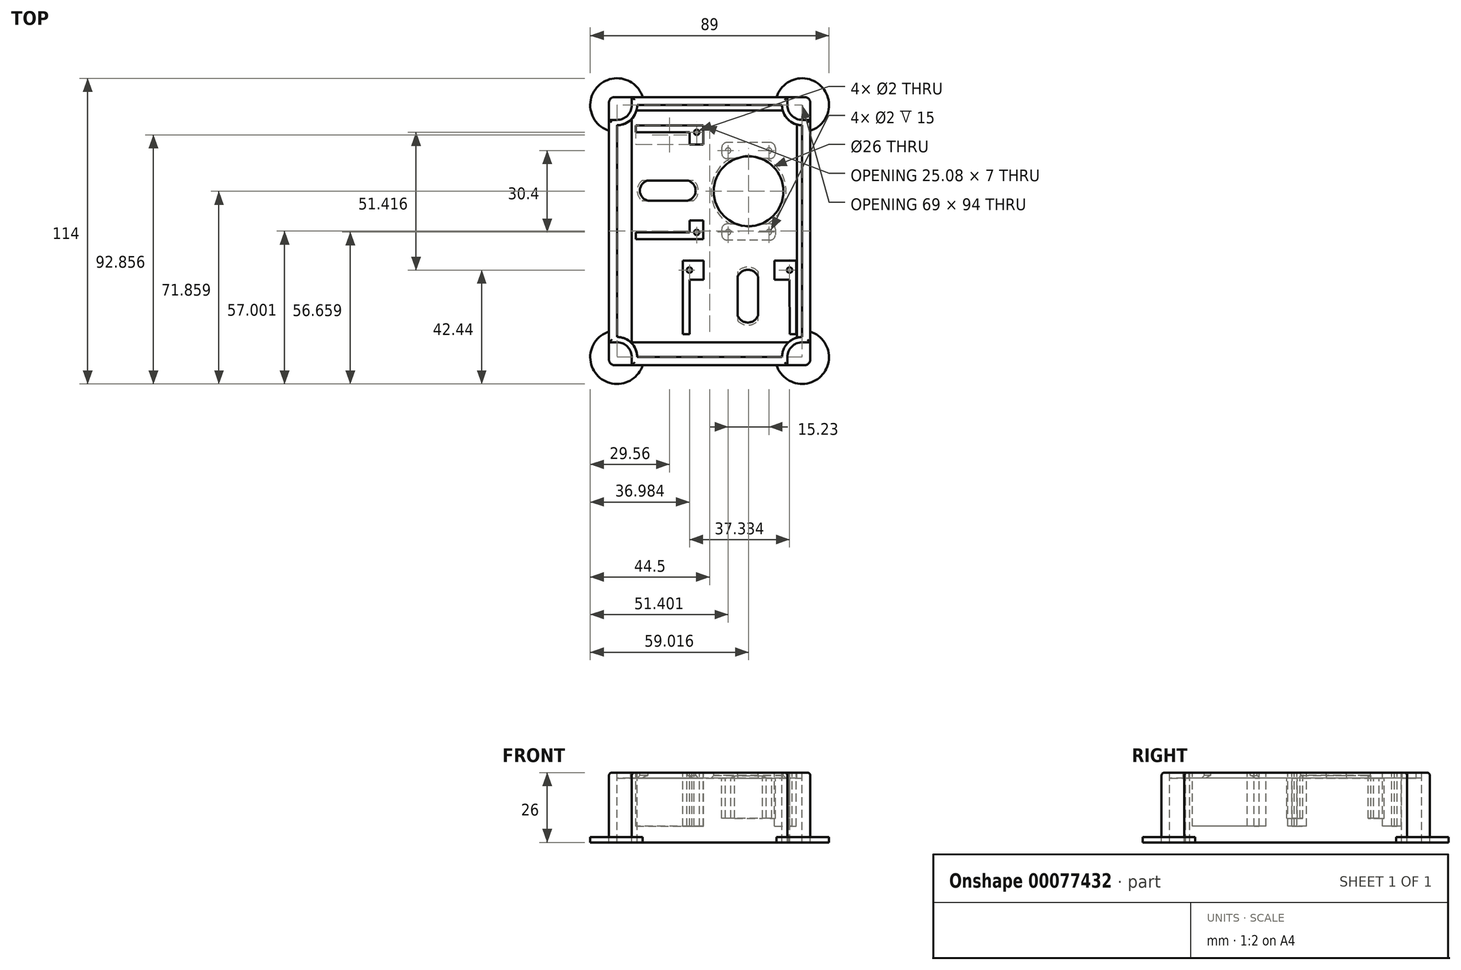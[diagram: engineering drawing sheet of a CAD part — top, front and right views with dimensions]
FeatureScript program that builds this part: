
annotation { "Feature Type Name" : "Feature", "Feature Type Description" : "" }
export const myFeature = defineFeature(function(context is Context, id is Id, definition is map)
    precondition{}
    {
        {
            var Q0;
            Q0=qCreatedBy(makeId("Top.planeOp"),FACE);
            var sketch = newSketch(context, id + "F0", { "sketchPlane" : qUnion([Q0])});
            skLineSegment(sketch, "E0.rect.bottom", {"start": v(-24.52, 14) * mm, "end": v(17.82, 14) * mm});
            skLineSegment(sketch, "E0.rect.top", {"start": v(-24.52, -14) * mm, "end": v(17.82, -14) * mm});
            skLineSegment(sketch, "E0.rect.right", {"start": v(17.82, 14) * mm, "end": v(17.82, -14) * mm});
            skPoint(sketch, "E0.rect.middle", {"position": v(0, 0) * mm});
            skLineSegment(sketch, "E1.rect.bottom", {"start": v(5.3, -4.4) * mm, "end": v(-5.3, -4.4) * mm, "construction": true});
            skLineSegment(sketch, "E1.rect.top", {"start": v(5.3, 6) * mm, "end": v(-5.3, 6) * mm, "construction": true});
            skLineSegment(sketch, "E1.rect.left", {"start": v(5.3, -4.4) * mm, "end": v(5.3, 6) * mm, "construction": true});
            skLineSegment(sketch, "E1.rect.right", {"start": v(-5.3, -4.4) * mm, "end": v(-5.3, 6) * mm, "construction": true});
            skPoint(sketch, "E1.rect.middle", {"position": v(0, 0.8) * mm});
            skLineSegment(sketch, "E2.bottom", {"start": v(-5.3, 6) * mm, "end": v(-3.9, 6) * mm});
            skLineSegment(sketch, "E2.top", {"start": v(-5.3, -4.4) * mm, "end": v(-3.9, -4.4) * mm});
            skLineSegment(sketch, "E2.left", {"start": v(-5.3, 6) * mm, "end": v(-5.3, -4.4) * mm});
            skLineSegment(sketch, "E2.right", {"start": v(-3.9, 6) * mm, "end": v(-3.9, -4.4) * mm});
            skLineSegment(sketch, "E3.1.MirrorCS", {"start": v(3.9, 6) * mm, "end": v(3.9, -4.4) * mm});
            skLineSegment(sketch, "E3.2.MirrorCS", {"start": v(5.3, -4.4) * mm, "end": v(3.9, -4.4) * mm});
            skLineSegment(sketch, "E3.3.MirrorCS", {"start": v(5.3, 6) * mm, "end": v(5.3, -4.4) * mm});
            skLineSegment(sketch, "E3.4.MirrorCS", {"start": v(5.3, 6) * mm, "end": v(3.9, 6) * mm});
            skLineSegment(sketch, "E4", {"start": v(11.9, -2.52) * mm, "end": v(11.9, -9.66) * mm, "construction": true});
            skLineSegment(sketch, "E5", {"start": v(0.13, -12.4) * mm, "end": v(12.65, -12.4) * mm, "construction": true});
            skLineSegment(sketch, "E6", {"start": v(5.3, 0.8) * mm, "end": v(11.55, 0.8) * mm, "construction": true});
            skCircle(sketch, "E7", {"center": v(11.9, -12.4) * mm, "radius": 1.6 * mm});
            skCircle(sketch, "E8", {"center": v(11.9, -12.4) * mm, "radius": 0.75 * mm});
            skLineSegment(sketch, "E9", {"start": v(-16.6, 11.88) * mm, "end": v(-16.6, 4.47) * mm, "construction": true});
            skLineSegment(sketch, "E10", {"start": v(-16.6, 4.47) * mm, "end": v(-16.6, 0.29) * mm, "construction": true});
            skLineSegment(sketch, "E11", {"start": v(-21.75, -2.4) * mm, "end": v(-11.5, -2.4) * mm, "construction": true});
            skCircle(sketch, "E12", {"center": v(-16.6, -2.4) * mm, "radius": 1.6 * mm});
            skCircle(sketch, "E13", {"center": v(-16.6, -2.4) * mm, "radius": 0.45 * mm});
            skLineSegment(sketch, "E14", {"start": v(-24.52, 14) * mm, "end": v(-24.52, -14) * mm});
            skPoint(sketch, "E15.orphan", {"position": v(-17.82, -14) * mm});
            skPoint(sketch, "E0.rect.left.start.orphan", {"position": v(-17.82, 14) * mm});
            skSolve(sketch);
        }
        {
            var Q0;
            Q0=makeQuery(id+"F0.imprint","IMPRINT",FACE,{"disambiguationData":[TD([[makeQuery(id+"F0.imprint","IMPRINT",EDGE,{"derivedFrom":sQuery(id+"F0.wireOp",EDGE,"E0.rect.bottom")}),-1.0]])]});
            var sketch = newSketch(context, id + "F1", { "sketchPlane" : qUnion([Q0])});
            skLineSegment(sketch, "E16.bottom", {"start": v(34.7, 72.06) * mm, "end": v(-30.3, 72.06) * mm});
            skLineSegment(sketch, "E16.top", {"start": v(34.7, -17.94) * mm, "end": v(-30.3, -17.94) * mm});
            skLineSegment(sketch, "E16.left", {"start": v(34.7, 72.06) * mm, "end": v(34.7, -17.94) * mm});
            skLineSegment(sketch, "E16.right", {"start": v(-30.3, 72.06) * mm, "end": v(-30.3, -17.94) * mm});
            skLineSegment(sketch, "E17.bottom", {"start": v(24.22, 56.92) * mm, "end": v(9.22, 56.92) * mm, "construction": true});
            skLineSegment(sketch, "E17.top", {"start": v(24.22, 26.92) * mm, "end": v(9.22, 26.92) * mm, "construction": true});
            skLineSegment(sketch, "E17.left", {"start": v(24.22, 56.92) * mm, "end": v(24.22, 26.92) * mm, "construction": true});
            skLineSegment(sketch, "E17.right", {"start": v(9.22, 56.92) * mm, "end": v(9.22, 26.92) * mm, "construction": true});
            skCircle(sketch, "E18", {"center": v(24.22, 56.92) * mm, "radius": 1 * mm});
            skArc(sketch, "E19", {"start": v(24.22, 54.67) * mm, "mid": v(26.47, 56.92) * mm, "end": v(24.22, 59.17) * mm});
            skCircle(sketch, "E20", {"center": v(9.22, 56.92) * mm, "radius": 1 * mm});
            skArc(sketch, "E21", {"start": v(9.22, 59.17) * mm, "mid": v(6.97, 56.92) * mm, "end": v(9.22, 54.67) * mm});
            skCircle(sketch, "E22", {"center": v(24.22, 26.92) * mm, "radius": 1 * mm});
            skArc(sketch, "E23", {"start": v(24.22, 24.67) * mm, "mid": v(26.47, 26.92) * mm, "end": v(24.22, 29.17) * mm});
            skCircle(sketch, "E24", {"center": v(9.22, 26.92) * mm, "radius": 1 * mm});
            skArc(sketch, "E25", {"start": v(9.22, 29.17) * mm, "mid": v(6.97, 26.92) * mm, "end": v(9.22, 24.67) * mm});
            skLineSegment(sketch, "E26", {"start": v(24.22, 54.67) * mm, "end": v(9.22, 54.67) * mm});
            skLineSegment(sketch, "E27", {"start": v(24.22, 29.17) * mm, "end": v(9.22, 29.17) * mm});
            skLineSegment(sketch, "E28.0.MirrorCS", {"start": v(24.22, 59.17) * mm, "end": v(9.22, 59.17) * mm});
            skLineSegment(sketch, "E29.0.MirrorCS", {"start": v(24.22, 24.67) * mm, "end": v(9.22, 24.67) * mm});
            skLineSegment(sketch, "E30", {"start": v(24.22, 56.92) * mm, "end": v(9.22, 26.92) * mm, "construction": true});
            skLineSegment(sketch, "E31", {"start": v(9.22, 56.92) * mm, "end": v(24.22, 26.92) * mm, "construction": true});
            skCircle(sketch, "E32", {"center": v(16.72, 41.92) * mm, "radius": 10 * mm});
            skLineSegment(sketch, "E33", {"start": v(16.72, 41.92) * mm, "end": v(-32.46, 41.92) * mm, "construction": true});
            skLineSegment(sketch, "E34", {"start": v(16.72, 41.92) * mm, "end": v(16.72, -38.62) * mm, "construction": true});
            skSolve(sketch);
        }
        {
            var Q0;
            Q0=qCreatedBy(makeId("Top.planeOp"),FACE);
            cPlane(context, id + "F2", {"entities" : qUnion([Q0]), "cplaneType" : CPlaneType.OFFSET, "offset" : 22.03 * mm, "width" : 150 * mm, "height" : 150 * mm});
        }
        {
            var Q0;
            Q0=qCreatedBy(makeId("Top.planeOp"),FACE);
            cPlane(context, id + "F3", {"entities" : qUnion([Q0]), "cplaneType" : CPlaneType.OFFSET, "offset" : 12.28 * mm, "width" : 150 * mm, "height" : 150 * mm});
        }
        {
            var Q0;
            Q0=qCreatedBy(id+"F3.planeOp",FACE);
            var sketch = newSketch(context, id + "F4", { "sketchPlane" : qUnion([Q0])});
            skLineSegment(sketch, "E35.0.0", {"start": v(34.7, 72.06) * mm, "end": v(34.7, -17.94) * mm});
            skLineSegment(sketch, "E35.0.1", {"start": v(34.7, 72.06) * mm, "end": v(-30.3, 72.06) * mm});
            skLineSegment(sketch, "E35.0.2", {"start": v(-30.3, 72.06) * mm, "end": v(-30.3, -17.94) * mm});
            skLineSegment(sketch, "E35.0.3", {"start": v(34.7, -17.94) * mm, "end": v(-30.3, -17.94) * mm});
            skLineSegment(sketch, "E36.bottom", {"start": v(-30.3, -17.94) * mm, "end": v(34.7, -17.94) * mm});
            skLineSegment(sketch, "E36.top", {"start": v(-30.3, 72.06) * mm, "end": v(34.7, 72.06) * mm});
            skLineSegment(sketch, "E36.left", {"start": v(-30.3, -17.94) * mm, "end": v(-30.3, 72.06) * mm});
            skLineSegment(sketch, "E36.right", {"start": v(34.7, -17.94) * mm, "end": v(34.7, 72.06) * mm});
            skSolve(sketch);
        }
        {
            var Q0;
            Q0=qCreatedBy(id+"F2.planeOp",FACE);
            var sketch = newSketch(context, id + "F5", { "sketchPlane" : qUnion([Q0])});
            skLineSegment(sketch, "E37.bottom", {"start": v(37.7, 77.06) * mm, "end": v(-33.3, 77.06) * mm});
            skLineSegment(sketch, "E37.top", {"start": v(37.7, -22.94) * mm, "end": v(-33.3, -22.94) * mm});
            skLineSegment(sketch, "E37.left", {"start": v(39.7, 75.06) * mm, "end": v(39.7, -20.94) * mm});
            skLineSegment(sketch, "E37.right", {"start": v(-35.3, 75.06) * mm, "end": v(-35.3, -20.94) * mm});
            skLineSegment(sketch, "E38.0", {"start": v(34.7, 72.06) * mm, "end": v(-30.3, 72.06) * mm});
            skLineSegment(sketch, "E38.1", {"start": v(-30.3, 72.06) * mm, "end": v(-30.3, -17.94) * mm});
            skLineSegment(sketch, "E38.2", {"start": v(34.7, -17.94) * mm, "end": v(-30.3, -17.94) * mm});
            skLineSegment(sketch, "E38.3", {"start": v(34.7, 72.06) * mm, "end": v(34.7, -17.94) * mm});
            skCircle(sketch, "E39", {"center": v(-30.3, 72.06) * mm, "radius": 1.25 * mm});
            skCircle(sketch, "E40", {"center": v(34.7, 72.06) * mm, "radius": 1.25 * mm});
            skCircle(sketch, "E41", {"center": v(-30.3, -17.94) * mm, "radius": 1.25 * mm});
            skCircle(sketch, "E42", {"center": v(34.7, -17.94) * mm, "radius": 1.25 * mm});
            skLineSegment(sketch, "E43.0", {"start": v(-32.3, 74.06) * mm, "end": v(-32.3, -19.94) * mm});
            skLineSegment(sketch, "E43.1", {"start": v(36.7, 74.06) * mm, "end": v(-32.3, 74.06) * mm});
            skLineSegment(sketch, "E43.2", {"start": v(36.7, 74.06) * mm, "end": v(36.7, -19.94) * mm});
            skLineSegment(sketch, "E43.3", {"start": v(36.7, -19.94) * mm, "end": v(-32.3, -19.94) * mm});
            skArc(sketch, "E44", {"start": v(-32.3, 68.56) * mm, "mid": v(-28.41, 70.17) * mm, "end": v(-26.8, 74.06) * mm});
            skArc(sketch, "E45", {"start": v(31.2, 74.06) * mm, "mid": v(32.81, 70.17) * mm, "end": v(36.7, 68.56) * mm});
            skArc(sketch, "E46", {"start": v(-26.8, -19.94) * mm, "mid": v(-28.41, -16.05) * mm, "end": v(-32.3, -14.44) * mm});
            skArc(sketch, "E47", {"start": v(36.7, -14.44) * mm, "mid": v(32.81, -16.05) * mm, "end": v(31.2, -19.94) * mm});
            skLineSegment(sketch, "E48", {"start": v(36.7, 68.56) * mm, "end": v(39.7, 68.56) * mm});
            skLineSegment(sketch, "E49", {"start": v(-32.3, 68.56) * mm, "end": v(-35.3, 68.56) * mm});
            skPoint(sketch, "E50.orphan", {"position": v(-35.3, 69.45) * mm});
            skLineSegment(sketch, "E51", {"start": v(-26.8, 74.06) * mm, "end": v(-26.8, -17.94) * mm});
            skLineSegment(sketch, "E52", {"start": v(-30.3, -14.44) * mm, "end": v(39.7, -14.44) * mm});
            skLineSegment(sketch, "E53", {"start": v(31.2, -17.94) * mm, "end": v(31.2, 77.06) * mm});
            skLineSegment(sketch, "E54", {"start": v(31.2, -19.94) * mm, "end": v(31.2, -22.94) * mm});
            skLineSegment(sketch, "E55", {"start": v(-32.3, -14.44) * mm, "end": v(-35.3, -14.44) * mm});
            skLineSegment(sketch, "E56.trimOffspring", {"start": v(-26.8, -19.94) * mm, "end": v(-26.8, -22.94) * mm});
            skLineSegment(sketch, "E57", {"start": v(-26.8, 74.06) * mm, "end": v(-26.8, 77.06) * mm});
            skPoint(sketch, "E58.visualSharp", {"position": v(-35.3, 77.06) * mm});
            skArc(sketch, "E58.filletArc", {"start": v(-33.3, 77.06) * mm, "mid": v(-34.71, 76.48) * mm, "end": v(-35.3, 75.06) * mm});
            skPoint(sketch, "E59.visualSharp", {"position": v(39.7, 77.06) * mm});
            skArc(sketch, "E59.filletArc", {"start": v(39.7, 75.06) * mm, "mid": v(39.11, 76.48) * mm, "end": v(37.7, 77.06) * mm});
            skPoint(sketch, "E60.visualSharp", {"position": v(-35.3, -22.94) * mm});
            skArc(sketch, "E60.filletArc", {"start": v(-35.3, -20.94) * mm, "mid": v(-34.71, -22.35) * mm, "end": v(-33.3, -22.94) * mm});
            skPoint(sketch, "E61.visualSharp", {"position": v(39.7, -22.94) * mm});
            skArc(sketch, "E61.filletArc", {"start": v(37.7, -22.94) * mm, "mid": v(39.11, -22.35) * mm, "end": v(39.7, -20.94) * mm});
            skArc(sketch, "E62", {"start": v(-22.76, 77.06) * mm, "mid": v(-39.37, 81.13) * mm, "end": v(-35.3, 64.52) * mm});
            skArc(sketch, "E63", {"start": v(39.7, 64.52) * mm, "mid": v(43.77, 81.13) * mm, "end": v(27.16, 77.06) * mm});
            skArc(sketch, "E64", {"start": v(27.16, -22.94) * mm, "mid": v(43.77, -27) * mm, "end": v(39.7, -10.4) * mm});
            skArc(sketch, "E65", {"start": v(-35.3, -10.4) * mm, "mid": v(-39.37, -27) * mm, "end": v(-22.76, -22.94) * mm});
            skSolve(sketch);
        }
        {
            var Q0;
            Q0=qCreatedBy(id+"F2.planeOp",FACE);
            var sketch = newSketch(context, id + "F6", { "sketchPlane" : qUnion([Q0])});
            skLineSegment(sketch, "E66.0", {"start": v(37.7, 77.06) * mm, "end": v(-33.3, 77.06) * mm});
            skLineSegment(sketch, "E66.1", {"start": v(37.7, -22.94) * mm, "end": v(-33.3, -22.94) * mm});
            skLineSegment(sketch, "E66.2", {"start": v(39.7, 75.06) * mm, "end": v(39.7, -20.94) * mm});
            skLineSegment(sketch, "E66.3", {"start": v(-35.3, 75.06) * mm, "end": v(-35.3, -20.94) * mm});
            skLineSegment(sketch, "E66.4", {"start": v(34.7, 72.06) * mm, "end": v(-30.3, 72.06) * mm});
            skLineSegment(sketch, "E66.5", {"start": v(-30.3, 72.06) * mm, "end": v(-30.3, -17.94) * mm});
            skLineSegment(sketch, "E66.6", {"start": v(34.7, -17.94) * mm, "end": v(-30.3, -17.94) * mm});
            skLineSegment(sketch, "E66.7", {"start": v(34.7, 72.06) * mm, "end": v(34.7, -17.94) * mm});
            skCircle(sketch, "E66.8", {"center": v(-30.3, 72.06) * mm, "radius": 1.25 * mm});
            skCircle(sketch, "E66.9", {"center": v(34.7, 72.06) * mm, "radius": 1.25 * mm});
            skCircle(sketch, "E66.10", {"center": v(-30.3, -17.94) * mm, "radius": 1.25 * mm});
            skCircle(sketch, "E66.11", {"center": v(34.7, -17.94) * mm, "radius": 1.25 * mm});
            skLineSegment(sketch, "E66.12", {"start": v(-32.3, 74.06) * mm, "end": v(-32.3, -19.94) * mm});
            skLineSegment(sketch, "E66.13", {"start": v(36.7, 74.06) * mm, "end": v(-32.3, 74.06) * mm});
            skLineSegment(sketch, "E66.14", {"start": v(36.7, 74.06) * mm, "end": v(36.7, -19.94) * mm});
            skLineSegment(sketch, "E66.15", {"start": v(36.7, -19.94) * mm, "end": v(-32.3, -19.94) * mm});
            skArc(sketch, "E66.16", {"start": v(-32.3, 68.56) * mm, "mid": v(-28.41, 70.17) * mm, "end": v(-26.8, 74.06) * mm});
            skArc(sketch, "E66.17", {"start": v(31.2, 74.06) * mm, "mid": v(32.81, 70.17) * mm, "end": v(36.7, 68.56) * mm});
            skArc(sketch, "E66.18", {"start": v(-26.8, -19.94) * mm, "mid": v(-28.41, -16.05) * mm, "end": v(-32.3, -14.44) * mm});
            skArc(sketch, "E66.19", {"start": v(36.7, -14.44) * mm, "mid": v(32.81, -16.05) * mm, "end": v(31.2, -19.94) * mm});
            skLineSegment(sketch, "E66.20", {"start": v(36.7, 68.56) * mm, "end": v(39.7, 68.56) * mm});
            skLineSegment(sketch, "E66.21", {"start": v(-32.3, 68.56) * mm, "end": v(-35.3, 68.56) * mm});
            skPoint(sketch, "E66.22", {"position": v(-35.3, 69.45) * mm});
            skLineSegment(sketch, "E66.23", {"start": v(-26.8, 72.06) * mm, "end": v(-26.8, -17.94) * mm});
            skLineSegment(sketch, "E66.24", {"start": v(-30.3, -14.44) * mm, "end": v(39.7, -14.44) * mm});
            skLineSegment(sketch, "E66.26", {"start": v(31.2, -19.94) * mm, "end": v(31.2, -22.94) * mm});
            skLineSegment(sketch, "E66.27", {"start": v(-32.3, -14.44) * mm, "end": v(-35.3, -14.44) * mm});
            skLineSegment(sketch, "E66.28", {"start": v(-26.8, -19.94) * mm, "end": v(-26.8, -22.94) * mm});
            skLineSegment(sketch, "E66.29", {"start": v(-26.8, 74.06) * mm, "end": v(-26.8, 77.06) * mm});
            skPoint(sketch, "E66.30", {"position": v(-35.3, 77.06) * mm});
            skArc(sketch, "E66.31", {"start": v(-33.3, 77.06) * mm, "mid": v(-34.71, 76.48) * mm, "end": v(-35.3, 75.06) * mm});
            skPoint(sketch, "E66.32", {"position": v(39.7, 77.06) * mm});
            skArc(sketch, "E66.33", {"start": v(39.7, 75.06) * mm, "mid": v(39.11, 76.48) * mm, "end": v(37.7, 77.06) * mm});
            skPoint(sketch, "E66.34", {"position": v(-35.3, -22.94) * mm});
            skArc(sketch, "E66.35", {"start": v(-35.3, -20.94) * mm, "mid": v(-34.71, -22.35) * mm, "end": v(-33.3, -22.94) * mm});
            skPoint(sketch, "E66.36", {"position": v(39.7, -22.94) * mm});
            skArc(sketch, "E66.37", {"start": v(37.7, -22.94) * mm, "mid": v(39.11, -22.35) * mm, "end": v(39.7, -20.94) * mm});
            skPoint(sketch, "E67.orphan", {"position": v(-26.8, 74.06) * mm});
            skLineSegment(sketch, "E68.trimOffspring", {"start": v(31.2, 74.06) * mm, "end": v(31.2, 77.06) * mm});
            skArc(sketch, "E69.0", {"start": v(-32.3, 66.56) * mm, "mid": v(-27, 68.76) * mm, "end": v(-24.8, 74.06) * mm});
            skArc(sketch, "E70.0", {"start": v(29.2, 74.06) * mm, "mid": v(31.4, 68.76) * mm, "end": v(36.7, 66.56) * mm});
            skArc(sketch, "E71.0", {"start": v(-24.8, -19.94) * mm, "mid": v(-27, -14.64) * mm, "end": v(-32.3, -12.44) * mm});
            skArc(sketch, "E72.0", {"start": v(36.7, -12.44) * mm, "mid": v(34.28, -12.84) * mm, "end": v(32.12, -14) * mm});
            skLineSegment(sketch, "E73.bottom", {"start": v(-5.32, 9) * mm, "end": v(0, 9) * mm});
            skLineSegment(sketch, "E73.left", {"start": v(-5.32, 9) * mm, "end": v(-5.32, -14) * mm});
            skLineSegment(sketch, "E73.right", {"start": v(32.02, 9) * mm, "end": v(32.02, -11.4) * mm});
            skLineSegment(sketch, "E74.left", {"start": v(-7.82, 14) * mm, "end": v(-7.82, 12.5) * mm});
            skLineSegment(sketch, "E75", {"start": v(-5.32, 9) * mm, "end": v(-5.32, 11.73) * mm, "construction": true});
            skLineSegment(sketch, "E76", {"start": v(32.02, 9) * mm, "end": v(32.02, 11.5) * mm, "construction": true});
            skLineSegment(sketch, "E77.bottom", {"start": v(-5.2, 63.92) * mm, "end": v(-25.28, 63.92) * mm});
            skLineSegment(sketch, "E77.top", {"start": v(-5.2, 26.58) * mm, "end": v(-25.28, 26.58) * mm});
            skLineSegment(sketch, "E77.left", {"start": v(-5.2, 63.92) * mm, "end": v(-5.2, 59.42) * mm});
            skLineSegment(sketch, "E78", {"start": v(-5.2, 45.99) * mm, "end": v(0, 45.99) * mm, "construction": true});
            skLineSegment(sketch, "E79", {"start": v(-2.6, 45.99) * mm, "end": v(-2.6, 24.96) * mm, "construction": true});
            skLineSegment(sketch, "E80", {"start": v(-2.6, 24.96) * mm, "end": v(-2.6, 64.48) * mm, "construction": true});
            skLineSegment(sketch, "E81", {"start": v(-5.2, 63.92) * mm, "end": v(-2.6, 63.92) * mm, "construction": true});
            skLineSegment(sketch, "E82", {"start": v(-5.2, 26.58) * mm, "end": v(-1.42, 26.58) * mm, "construction": true});
            skCircle(sketch, "E83", {"center": v(-2.6, 63.92) * mm, "radius": 1 * mm});
            skLineSegment(sketch, "E84", {"start": v(-25.28, 66.42) * mm, "end": v(-25.28, 63.92) * mm});
            skLineSegment(sketch, "E85.trimOffspring", {"start": v(-25.28, 26.58) * mm, "end": v(-25.28, 24.08) * mm});
            skLineSegment(sketch, "E86", {"start": v(-7.82, -11.39) * mm, "end": v(34.52, -11.39) * mm});
            skLineSegment(sketch, "E87.left", {"start": v(-7.82, 14) * mm, "end": v(-7.82, 16) * mm});
            skLineSegment(sketch, "E87.right", {"start": v(34.52, 14) * mm, "end": v(34.52, 16) * mm});
            skLineSegment(sketch, "E88", {"start": v(12.87, 12.5) * mm, "end": v(12.87, 16) * mm, "construction": true});
            skLineSegment(sketch, "E89", {"start": v(12.87, 12.5) * mm, "end": v(32.96, 12.5) * mm, "construction": true});
            skLineSegment(sketch, "E90", {"start": v(32.96, 12.5) * mm, "end": v(-7.82, 12.5) * mm, "construction": true});
            skCircle(sketch, "E91", {"center": v(-5.32, 12.5) * mm, "radius": 1 * mm});
            skCircle(sketch, "E92", {"center": v(32.02, 12.5) * mm, "radius": 1 * mm});
            skLineSegment(sketch, "E93.left", {"start": v(0, 16) * mm, "end": v(0, 9) * mm});
            skLineSegment(sketch, "E93.right", {"start": v(26.43, 16) * mm, "end": v(26.43, 9) * mm});
            skLineSegment(sketch, "E94.trimOffspring", {"start": v(-0.2, 31.08) * mm, "end": v(-0.2, 24.08) * mm});
            skLineSegment(sketch, "E95.trimOffspring", {"start": v(26.43, 9) * mm, "end": v(32.02, 9) * mm});
            skPoint(sketch, "E96.orphan", {"position": v(12.87, 9) * mm});
            skLineSegment(sketch, "E97", {"start": v(32.02, 9) * mm, "end": v(32.1, -11.4) * mm});
            skLineSegment(sketch, "E98", {"start": v(34.52, 14) * mm, "end": v(34.52, -11.39) * mm});
            skLineSegment(sketch, "E99", {"start": v(34.52, -11.39) * mm, "end": v(32.02, -11.4) * mm});
            skLineSegment(sketch, "E100", {"start": v(26.43, 14) * mm, "end": v(26.43, 16) * mm});
            skLineSegment(sketch, "E101", {"start": v(-25.28, 26.58) * mm, "end": v(-5.2, 26.58) * mm});
            skLineSegment(sketch, "E102", {"start": v(-5.2, 26.58) * mm, "end": v(-5.2, 31.08) * mm});
            skLineSegment(sketch, "E103", {"start": v(-25.28, 66.42) * mm, "end": v(-0.2, 66.42) * mm});
            skLineSegment(sketch, "E104", {"start": v(-0.2, 66.42) * mm, "end": v(-0.2, 59.42) * mm});
            skLineSegment(sketch, "E105", {"start": v(-25.28, 24.08) * mm, "end": v(-0.2, 24.08) * mm});
            skLineSegment(sketch, "E106", {"start": v(-25.28, 24.08) * mm, "end": v(-28.2, 24.08) * mm, "construction": true});
            skPoint(sketch, "E107.orphan", {"position": v(-7.82, -14) * mm});
            skLineSegment(sketch, "E108", {"start": v(-7.82, -11.39) * mm, "end": v(-7.82, -14) * mm});
            skLineSegment(sketch, "E109", {"start": v(-7.82, -14) * mm, "end": v(-5.32, -14) * mm});
            skLineSegment(sketch, "E110", {"start": v(-7.82, -14) * mm, "end": v(-7.82, -11.39) * mm});
            skLineSegment(sketch, "E111", {"start": v(-7.82, -11.39) * mm, "end": v(-7.82, 12.5) * mm});
            skLineSegment(sketch, "E112", {"start": v(-7.82, 12.5) * mm, "end": v(-7.82, -14) * mm});
            skLineSegment(sketch, "E113", {"start": v(-5.32, -14) * mm, "end": v(-5.32, 9) * mm});
            skLineSegment(sketch, "E114", {"start": v(0, 9) * mm, "end": v(0, 14) * mm});
            skLineSegment(sketch, "E115", {"start": v(0, 9) * mm, "end": v(0, 16) * mm});
            skLineSegment(sketch, "E116", {"start": v(0, 16) * mm, "end": v(-7.82, 16) * mm});
            skArc(sketch, "E117.trimOffspring", {"start": v(31.6, -14.44) * mm, "mid": v(29.83, -16.94) * mm, "end": v(29.2, -19.94) * mm});
            skPoint(sketch, "E118.0.end.orphan", {"position": v(34.52, -12.76) * mm});
            skLineSegment(sketch, "E119", {"start": v(31.6, -14.44) * mm, "end": v(32.12, -14) * mm});
            skLineSegment(sketch, "E120", {"start": v(-25.28, 66.42) * mm, "end": v(-28.2, 66.42) * mm, "construction": true});
            skLineSegment(sketch, "E121.trimOffspring", {"start": v(26.43, 16) * mm, "end": v(34.52, 16) * mm});
            skLineSegment(sketch, "E122", {"start": v(26.43, 9) * mm, "end": v(26.43, 16) * mm});
            skLineSegment(sketch, "E123", {"start": v(-5.2, 31.08) * mm, "end": v(0, 31.08) * mm});
            skLineSegment(sketch, "E124.trimOffspring", {"start": v(-5.2, 31.08) * mm, "end": v(-5.2, 26.58) * mm});
            skLineSegment(sketch, "E125", {"start": v(-0.2, 59.42) * mm, "end": v(-5.2, 59.42) * mm});
            skCircle(sketch, "E126", {"center": v(-2.6, 26.58) * mm, "radius": 1 * mm});
            skSolve(sketch);
        }
        {
            var Q0;
            {var subQ1=sQuery(id+"F6.wireOp",EDGE,"E66.23");var subQ3=sQuery(id+"F6.wireOp",EDGE,"E66.6");var subQ5=makeQuery(id+"F6.imprint","INTERSECT",VERTEX,{"derivedFrom":[subQ3,subQ1]});Q0=makeQuery(id+"F6.imprint","IMPRINT",FACE,{"disambiguationData":[TD([[makeQuery(id+"F6.imprint","IMPRINT",EDGE,{"disambiguationData":[TD([[subQ5,1.0]])],"derivedFrom":subQ3}),-1.0]])]});}
            var Q1;
            {var subQ1=sQuery(id+"F6.wireOp",EDGE,"E66.23");var subQ3=sQuery(id+"F6.wireOp",EDGE,"E66.6");var subQ5=makeQuery(id+"F6.imprint","INTERSECT",VERTEX,{"derivedFrom":[subQ3,subQ1]});Q1=makeQuery(id+"F6.imprint","IMPRINT",FACE,{"disambiguationData":[TD([[makeQuery(id+"F6.imprint","IMPRINT",EDGE,{"disambiguationData":[TD([[subQ5,1.0]])],"derivedFrom":subQ3}),-1.0]])]});}
            var Q2;
            {var subQ3=sQuery(id+"F6.wireOp",EDGE,"E66.29");Q2=makeQuery(id+"F6.imprint","IMPRINT",FACE,{"disambiguationData":[TD([[makeQuery(id+"F6.imprint","IMPRINT",EDGE,{"derivedFrom":subQ3}),-1.0]])]});}
            var Q3;
            {var subQ1=sQuery(id+"F6.wireOp",EDGE,"E66.26");Q3=makeQuery(id+"F6.imprint","IMPRINT",FACE,{"disambiguationData":[TD([[makeQuery(id+"F6.imprint","IMPRINT",EDGE,{"derivedFrom":subQ1}),-1.0]])]});}
            var Q4;
            {var subQ5=sQuery(id+"F6.wireOp",EDGE,"E66.20");Q4=makeQuery(id+"F6.imprint","IMPRINT",FACE,{"disambiguationData":[TD([[makeQuery(id+"F6.imprint","IMPRINT",EDGE,{"derivedFrom":subQ5}),-1.0]])]});}
            var Q5;
            {var subQ1=sQuery(id+"F6.wireOp",EDGE,"E66.21");Q5=makeQuery(id+"F6.imprint","IMPRINT",FACE,{"disambiguationData":[TD([[makeQuery(id+"F6.imprint","IMPRINT",EDGE,{"derivedFrom":subQ1}),1.0]])]});}
            var Q6;
            {var subQ1=sQuery(id+"F6.wireOp",EDGE,"E66.5");var subQ5=sQuery(id+"F6.wireOp",EDGE,"E66.16");var subQ6=makeQuery(id+"F6.imprint","INTERSECT",VERTEX,{"derivedFrom":[subQ1,subQ5]});Q6=makeQuery(id+"F6.imprint","IMPRINT",FACE,{"disambiguationData":[TD([[makeQuery(id+"F6.imprint","IMPRINT",EDGE,{"disambiguationData":[TD([[subQ6,-1.0]])],"derivedFrom":subQ1}),-1.0]])]});}
            var Q7;
            {var subQ1=sQuery(id+"F6.wireOp",EDGE,"E66.23");var subQ5=sQuery(id+"F6.wireOp",EDGE,"E66.4");var subQ6=makeQuery(id+"F6.imprint","INTERSECT",VERTEX,{"derivedFrom":[subQ5,subQ1]});Q7=makeQuery(id+"F6.imprint","IMPRINT",FACE,{"disambiguationData":[TD([[makeQuery(id+"F6.imprint","IMPRINT",EDGE,{"disambiguationData":[TD([[subQ6,-1.0]])],"derivedFrom":subQ5}),1.0]])]});}
            var Q8;
            {var subQ1=sQuery(id+"F6.wireOp",EDGE,"E66.23");var subQ3=sQuery(id+"F6.wireOp",EDGE,"E66.4");var subQ5=makeQuery(id+"F6.imprint","INTERSECT",VERTEX,{"derivedFrom":[subQ3,subQ1]});Q8=makeQuery(id+"F6.imprint","IMPRINT",FACE,{"disambiguationData":[TD([[makeQuery(id+"F6.imprint","IMPRINT",EDGE,{"disambiguationData":[TD([[subQ5,1.0]])],"derivedFrom":subQ3}),1.0]])]});}
            var Q9;
            {var subQ1=sQuery(id+"F6.wireOp",EDGE,"E66.4");var subQ7=makeQuery(id+"F6.imprint","INTERSECT",VERTEX,{"derivedFrom":[subQ1,sQuery(id+"F6.wireOp",EDGE,"E66.23")]});Q9=makeQuery(id+"F6.imprint","IMPRINT",FACE,{"disambiguationData":[TD([[makeQuery(id+"F6.imprint","IMPRINT",EDGE,{"disambiguationData":[TD([[subQ7,1.0]])],"derivedFrom":subQ1}),-1.0]])]});}
            var Q10;
            {var subQ1=sQuery(id+"F6.wireOp",EDGE,"E66.4");var subQ7=makeQuery(id+"F6.imprint","INTERSECT",VERTEX,{"derivedFrom":[subQ1,sQuery(id+"F6.wireOp",EDGE,"E66.23")]});Q10=makeQuery(id+"F6.imprint","IMPRINT",FACE,{"disambiguationData":[TD([[makeQuery(id+"F6.imprint","IMPRINT",EDGE,{"disambiguationData":[TD([[subQ7,1.0]])],"derivedFrom":subQ1}),-1.0]])]});}
            var Q11;
            {var subQ1=sQuery(id+"F6.wireOp",EDGE,"E66.23");var subQ3=sQuery(id+"F6.wireOp",EDGE,"E66.4");var subQ5=makeQuery(id+"F6.imprint","INTERSECT",VERTEX,{"derivedFrom":[subQ3,subQ1]});Q11=makeQuery(id+"F6.imprint","IMPRINT",FACE,{"disambiguationData":[TD([[makeQuery(id+"F6.imprint","IMPRINT",EDGE,{"disambiguationData":[TD([[subQ5,1.0]])],"derivedFrom":subQ3}),1.0]])]});}
            var Q12;
            {var subQ1=sQuery(id+"F6.wireOp",EDGE,"E66.23");var subQ3=sQuery(id+"F6.wireOp",EDGE,"E66.4");var subQ5=makeQuery(id+"F6.imprint","INTERSECT",VERTEX,{"derivedFrom":[subQ3,subQ1]});Q12=makeQuery(id+"F6.imprint","IMPRINT",FACE,{"disambiguationData":[TD([[makeQuery(id+"F6.imprint","IMPRINT",EDGE,{"disambiguationData":[TD([[subQ5,1.0]])],"derivedFrom":subQ3}),1.0]])]});}
            var Q13;
            {var subQ1=sQuery(id+"F6.wireOp",EDGE,"E66.7");var subQ5=sQuery(id+"F6.wireOp",EDGE,"E66.17");var subQ6=makeQuery(id+"F6.imprint","INTERSECT",VERTEX,{"derivedFrom":[subQ1,subQ5]});Q13=makeQuery(id+"F6.imprint","IMPRINT",FACE,{"disambiguationData":[TD([[makeQuery(id+"F6.imprint","IMPRINT",EDGE,{"disambiguationData":[TD([[subQ6,-1.0]])],"derivedFrom":subQ1}),1.0]])]});}
            var Q14;
            {var subQ0=sQuery(id+"F6.wireOp",EDGE,"E72.0");var subQ1=sQuery(id+"F6.wireOp",EDGE,"E66.7");var subQ2=makeQuery(id+"F6.imprint","INTERSECT",VERTEX,{"derivedFrom":[subQ1,subQ0]});Q14=makeQuery(id+"F6.imprint","IMPRINT",FACE,{"disambiguationData":[TD([[makeQuery(id+"F6.imprint","IMPRINT",EDGE,{"disambiguationData":[TD([[subQ2,-1.0]])],"derivedFrom":subQ1}),1.0]])]});}
            var Q15;
            {var subQ0=sQuery(id+"F6.wireOp",EDGE,"E119");Q15=makeQuery(id+"F6.imprint","IMPRINT",FACE,{"disambiguationData":[TD([[makeQuery(id+"F6.imprint","IMPRINT",EDGE,{"derivedFrom":subQ0}),-1.0]])]});}
            var Q16;
            {var subQ1=sQuery(id+"F6.wireOp",EDGE,"E66.23");var subQ3=sQuery(id+"F6.wireOp",EDGE,"E66.6");var subQ5=makeQuery(id+"F6.imprint","INTERSECT",VERTEX,{"derivedFrom":[subQ3,subQ1]});Q16=makeQuery(id+"F6.imprint","IMPRINT",FACE,{"disambiguationData":[TD([[makeQuery(id+"F6.imprint","IMPRINT",EDGE,{"disambiguationData":[TD([[subQ5,1.0]])],"derivedFrom":subQ3}),-1.0]])]});}
            var Q17;
            {var subQ1=sQuery(id+"F6.wireOp",EDGE,"E66.6");var subQ8=makeQuery(id+"F6.imprint","INTERSECT",VERTEX,{"derivedFrom":[subQ1,sQuery(id+"F6.wireOp",EDGE,"E66.23")]});Q17=makeQuery(id+"F6.imprint","IMPRINT",FACE,{"disambiguationData":[TD([[makeQuery(id+"F6.imprint","IMPRINT",EDGE,{"disambiguationData":[TD([[subQ8,1.0]])],"derivedFrom":subQ1}),1.0]])]});}
            var Q18;
            {var subQ1=sQuery(id+"F6.wireOp",EDGE,"E66.6");var subQ8=makeQuery(id+"F6.imprint","INTERSECT",VERTEX,{"derivedFrom":[subQ1,sQuery(id+"F6.wireOp",EDGE,"E66.23")]});Q18=makeQuery(id+"F6.imprint","IMPRINT",FACE,{"disambiguationData":[TD([[makeQuery(id+"F6.imprint","IMPRINT",EDGE,{"disambiguationData":[TD([[subQ8,1.0]])],"derivedFrom":subQ1}),1.0]])]});}
            var Q19;
            {var subQ1=sQuery(id+"F6.wireOp",EDGE,"E66.23");var subQ3=sQuery(id+"F6.wireOp",EDGE,"E66.6");var subQ5=makeQuery(id+"F6.imprint","INTERSECT",VERTEX,{"derivedFrom":[subQ3,subQ1]});Q19=makeQuery(id+"F6.imprint","IMPRINT",FACE,{"disambiguationData":[TD([[makeQuery(id+"F6.imprint","IMPRINT",EDGE,{"disambiguationData":[TD([[subQ5,1.0]])],"derivedFrom":subQ3}),-1.0]])]});}
            var Q20;
            {var subQ1=sQuery(id+"F6.wireOp",EDGE,"E66.24");var subQ5=sQuery(id+"F6.wireOp",EDGE,"E66.5");var subQ6=makeQuery(id+"F6.imprint","INTERSECT",VERTEX,{"derivedFrom":[subQ5,subQ1]});Q20=makeQuery(id+"F6.imprint","IMPRINT",FACE,{"disambiguationData":[TD([[makeQuery(id+"F6.imprint","IMPRINT",EDGE,{"disambiguationData":[TD([[subQ6,-1.0]])],"derivedFrom":subQ5}),1.0]])]});}
            var Q21;
            {var subQ1=sQuery(id+"F6.wireOp",EDGE,"E66.24");var subQ3=sQuery(id+"F6.wireOp",EDGE,"E66.5");var subQ5=makeQuery(id+"F6.imprint","INTERSECT",VERTEX,{"derivedFrom":[subQ3,subQ1]});Q21=makeQuery(id+"F6.imprint","IMPRINT",FACE,{"disambiguationData":[TD([[makeQuery(id+"F6.imprint","IMPRINT",EDGE,{"disambiguationData":[TD([[subQ5,1.0]])],"derivedFrom":subQ3}),1.0]])]});}
            var Q22;
            {var subQ1=sQuery(id+"F6.wireOp",EDGE,"E66.5");var subQ8=makeQuery(id+"F6.imprint","INTERSECT",VERTEX,{"derivedFrom":[subQ1,sQuery(id+"F6.wireOp",EDGE,"E66.24")]});Q22=makeQuery(id+"F6.imprint","IMPRINT",FACE,{"disambiguationData":[TD([[makeQuery(id+"F6.imprint","IMPRINT",EDGE,{"disambiguationData":[TD([[subQ8,1.0]])],"derivedFrom":subQ1}),-1.0]])]});}
            var Q23;
            {var subQ1=sQuery(id+"F6.wireOp",EDGE,"E66.6");var subQ7=sQuery(id+"F6.wireOp",EDGE,"E66.19");var subQ9=makeQuery(id+"F6.imprint","INTERSECT",VERTEX,{"derivedFrom":[subQ1,subQ7]});Q23=makeQuery(id+"F6.imprint","IMPRINT",FACE,{"disambiguationData":[TD([[makeQuery(id+"F6.imprint","IMPRINT",EDGE,{"disambiguationData":[TD([[subQ9,-1.0]])],"derivedFrom":subQ1}),-1.0]])]});}
            var Q24;
            {var subQ1=sQuery(id+"F6.wireOp",EDGE,"E66.6");var subQ5=sQuery(id+"F6.wireOp",EDGE,"E66.19");var subQ6=makeQuery(id+"F6.imprint","INTERSECT",VERTEX,{"derivedFrom":[subQ1,subQ5]});Q24=makeQuery(id+"F6.imprint","IMPRINT",FACE,{"disambiguationData":[TD([[makeQuery(id+"F6.imprint","IMPRINT",EDGE,{"disambiguationData":[TD([[subQ6,-1.0]])],"derivedFrom":subQ1}),1.0]])]});}
            var Q25;
            {var subQ1=sQuery(id+"F6.wireOp",EDGE,"E66.7");var subQ3=sQuery(id+"F6.wireOp",EDGE,"E66.24");var subQ5=makeQuery(id+"F6.imprint","INTERSECT",VERTEX,{"derivedFrom":[subQ1,subQ3]});Q25=makeQuery(id+"F6.imprint","IMPRINT",FACE,{"disambiguationData":[TD([[makeQuery(id+"F6.imprint","IMPRINT",EDGE,{"disambiguationData":[TD([[subQ5,-1.0]])],"derivedFrom":subQ1}),1.0]])]});}
            var Q26;
            {var subQ3=sQuery(id+"F6.wireOp",EDGE,"E66.4");var subQ5=sQuery(id+"F6.wireOp",EDGE,"E66.17");var subQ7=makeQuery(id+"F6.imprint","INTERSECT",VERTEX,{"derivedFrom":[subQ3,subQ5]});Q26=makeQuery(id+"F6.imprint","IMPRINT",FACE,{"disambiguationData":[TD([[makeQuery(id+"F6.imprint","IMPRINT",EDGE,{"disambiguationData":[TD([[subQ7,-1.0]])],"derivedFrom":subQ3}),1.0]])]});}
            var Q27;
            {var subQ1=sQuery(id+"F6.wireOp",EDGE,"E66.4");var subQ5=sQuery(id+"F6.wireOp",EDGE,"E66.17");var subQ6=makeQuery(id+"F6.imprint","INTERSECT",VERTEX,{"derivedFrom":[subQ1,subQ5]});Q27=makeQuery(id+"F6.imprint","IMPRINT",FACE,{"disambiguationData":[TD([[makeQuery(id+"F6.imprint","IMPRINT",EDGE,{"disambiguationData":[TD([[subQ6,-1.0]])],"derivedFrom":subQ1}),-1.0]])]});}
            extrude(context, id + "F7", {"entities" : qUnion([Q0, Q1, Q2, Q3, Q4, Q5, Q6, Q7, Q8, Q9, Q10, Q11, Q12, Q13, Q14, Q15, Q16, Q17, Q18, Q19, Q20, Q21, Q22, Q23, Q24, Q25, Q26, Q27]), "oppositeDirection" : true, "depth" : 26 * mm});
        }
        {
            var Q0;
            Q0=makeQuery(id+"F7.opExtrude","CAP_FACE",FACE,{"disambiguationData":[OSD([sQuery(id+"F6.wireOp",EDGE,"E66.0"),sQuery(id+"F6.wireOp",EDGE,"E66.1"),sQuery(id+"F6.wireOp",EDGE,"E66.2"),sQuery(id+"F6.wireOp",EDGE,"E66.3"),sQuery(id+"F6.wireOp",EDGE,"E66.12"),sQuery(id+"F6.wireOp",EDGE,"E66.13"),sQuery(id+"F6.wireOp",EDGE,"E66.14"),sQuery(id+"F6.wireOp",EDGE,"E66.15"),sQuery(id+"F6.wireOp",EDGE,"E66.16"),sQuery(id+"F6.wireOp",EDGE,"E66.17"),sQuery(id+"F6.wireOp",EDGE,"E66.18"),sQuery(id+"F6.wireOp",EDGE,"E66.19"),sQuery(id+"F6.wireOp",EDGE,"E66.20"),sQuery(id+"F6.wireOp",EDGE,"E66.21"),sQuery(id+"F6.wireOp",EDGE,"E66.24"),sQuery(id+"F6.wireOp",EDGE,"E66.26"),sQuery(id+"F6.wireOp",EDGE,"E66.27"),sQuery(id+"F6.wireOp",EDGE,"E66.28"),sQuery(id+"F6.wireOp",EDGE,"E66.29"),sQuery(id+"F6.wireOp",EDGE,"E68.trimOffspring"),sQuery(id+"F6.wireOp",EDGE,"E69.0"),sQuery(id+"F6.wireOp",EDGE,"E70.0"),sQuery(id+"F6.wireOp",EDGE,"E71.0"),sQuery(id+"F6.wireOp",EDGE,"E72.0"),sQuery(id+"F6.wireOp",EDGE,"E117.trimOffspring"),sQuery(id+"F6.wireOp",EDGE,"E119")])],"isStart":false});
            var sketch = newSketch(context, id + "F8", { "sketchPlane" : qUnion([Q0])});
            skLineSegment(sketch, "E127.0", {"start": v(37.7, -77.06) * mm, "end": v(-33.3, -77.06) * mm});
            skArc(sketch, "E127.1", {"start": v(-33.3, -77.06) * mm, "mid": v(-34.71, -76.48) * mm, "end": v(-35.3, -75.06) * mm});
            skLineSegment(sketch, "E127.2", {"start": v(-35.3, -75.06) * mm, "end": v(-35.3, 20.94) * mm});
            skArc(sketch, "E127.3", {"start": v(39.7, -75.06) * mm, "mid": v(39.11, -76.48) * mm, "end": v(37.7, -77.06) * mm});
            skLineSegment(sketch, "E127.4", {"start": v(39.7, -75.06) * mm, "end": v(39.7, 20.94) * mm});
            skArc(sketch, "E127.5", {"start": v(37.7, 22.94) * mm, "mid": v(39.11, 22.35) * mm, "end": v(39.7, 20.94) * mm});
            skLineSegment(sketch, "E127.6", {"start": v(37.7, 22.94) * mm, "end": v(-33.3, 22.94) * mm});
            skArc(sketch, "E127.7", {"start": v(-35.3, 20.94) * mm, "mid": v(-34.71, 22.35) * mm, "end": v(-33.3, 22.94) * mm});
            skArc(sketch, "E128.0.0", {"start": v(29.47, -72.06) * mm, "mid": v(43.93, -76.06) * mm, "end": v(29.47, -72.06) * mm});
            skLineSegment(sketch, "E128.0.1", {"start": v(29.47, -72.06) * mm, "end": v(-25.07, -72.06) * mm});
            skArc(sketch, "E128.0.2", {"start": v(-26.8, -68.96) * mm, "mid": v(-25.75, -70.4) * mm, "end": v(-25.07, -72.06) * mm});
            skLineSegment(sketch, "E128.0.3", {"start": v(-26.8, -68.96) * mm, "end": v(-26.8, 14.44) * mm});
            skLineSegment(sketch, "E128.0.4", {"start": v(-26.8, 14.44) * mm, "end": v(-26.8, 14.44) * mm});
            skCircle(sketch, "E129.0", {"center": v(34.7, -72.06) * mm, "radius": 1.25 * mm});
            skCircle(sketch, "E129.1", {"center": v(-30.3, -72.06) * mm, "radius": 1.25 * mm});
            skCircle(sketch, "E129.2", {"center": v(34.7, 17.94) * mm, "radius": 1.25 * mm});
            skCircle(sketch, "E129.3", {"center": v(-30.3, 17.94) * mm, "radius": 1.25 * mm});
            skArc(sketch, "E130.0", {"start": v(-35.3, 10.4) * mm, "mid": v(-39.37, 27) * mm, "end": v(-22.76, 22.94) * mm});
            skArc(sketch, "E130.1", {"start": v(27.16, 22.94) * mm, "mid": v(43.77, 27) * mm, "end": v(39.7, 10.4) * mm});
            skArc(sketch, "E130.2", {"start": v(39.7, -64.52) * mm, "mid": v(43.77, -81.13) * mm, "end": v(27.16, -77.06) * mm});
            skArc(sketch, "E130.3", {"start": v(-22.76, -77.06) * mm, "mid": v(-39.37, -81.13) * mm, "end": v(-35.3, -64.52) * mm});
            skSolve(sketch);
        }
        {
            var Q0;
            {var subQ1=sQuery(id+"F8.wireOp",EDGE,"E128.0.0");Q0=makeQuery(id+"F8.imprint","IMPRINT",FACE,{"disambiguationData":[TD([[makeQuery(id+"F8.imprint","IMPRINT",EDGE,{"derivedFrom":subQ1}),-1.0]])]});}
            var Q1;
            {var subQ3=sQuery(id+"F8.wireOp",EDGE,"E127.5");Q1=makeQuery(id+"F8.imprint","IMPRINT",FACE,{"disambiguationData":[TD([[makeQuery(id+"F8.imprint","IMPRINT",EDGE,{"derivedFrom":subQ3}),-1.0]])]});}
            var Q2;
            {var subQ2=sQuery(id+"F8.wireOp",EDGE,"E127.7");Q2=makeQuery(id+"F8.imprint","IMPRINT",FACE,{"disambiguationData":[TD([[makeQuery(id+"F8.imprint","IMPRINT",EDGE,{"derivedFrom":subQ2}),-1.0]])]});}
            var Q3;
            {var subQ3=sQuery(id+"F8.wireOp",EDGE,"E127.3");Q3=makeQuery(id+"F8.imprint","IMPRINT",FACE,{"disambiguationData":[TD([[makeQuery(id+"F8.imprint","IMPRINT",EDGE,{"derivedFrom":subQ3}),-1.0]])]});}
            var Q4;
            {var subQ3=sQuery(id+"F8.wireOp",EDGE,"E127.1");Q4=makeQuery(id+"F8.imprint","IMPRINT",FACE,{"disambiguationData":[TD([[makeQuery(id+"F8.imprint","IMPRINT",EDGE,{"derivedFrom":subQ3}),-1.0]])]});}
            extrude(context, id + "F9", {"entities" : qUnion([Q0, Q1, Q2, Q3, Q4]), "operationType" : NewBodyOperationType.ADD, "oppositeDirection" : true, "depth" : 2 * mm});
        }
        {
            var Q0;
            Q0=qCreatedBy(id+"F2.planeOp",FACE);
            cPlane(context, id + "F10", {"entities" : qUnion([Q0]), "cplaneType" : CPlaneType.OFFSET, "offset" : 3 * mm, "oppositeDirection" : true, "width" : 150 * mm, "height" : 150 * mm});
        }
        {
            var Q0;
            {var subQ14=sQuery(id+"F6.wireOp",EDGE,"E73.bottom");Q0=makeQuery(id+"F6.imprint","IMPRINT",FACE,{"disambiguationData":[TD([[makeQuery(id+"F6.imprint","IMPRINT",EDGE,{"derivedFrom":subQ14}),-1.0]])]});}
            var sketch = newSketch(context, id + "F11", { "sketchPlane" : qUnion([Q0])});
            skCircle(sketch, "E131.4", {"center": v(16.72, 41.92) * mm, "radius": 13 * mm});
            skLineSegment(sketch, "E132.bottom", {"start": v(-5.69, 45.67) * mm, "end": v(-21.12, 45.67) * mm, "construction": true});
            skLineSegment(sketch, "E132.top", {"start": v(-5.69, 38.67) * mm, "end": v(-21.12, 38.67) * mm, "construction": true});
            skLineSegment(sketch, "E132.left", {"start": v(-5.69, 45.67) * mm, "end": v(-5.69, 38.67) * mm});
            skLineSegment(sketch, "E133", {"start": v(-5.69, 42.17) * mm, "end": v(-21.12, 42.17) * mm, "construction": true});
            skLineSegment(sketch, "E134", {"start": v(-6.06, 45.92) * mm, "end": v(-20.75, 45.92) * mm});
            skLineSegment(sketch, "E135", {"start": v(-5.69, 38.42) * mm, "end": v(-21.12, 38.42) * mm});
            skLineSegment(sketch, "E136", {"start": v(-6.06, 45.92) * mm, "end": v(-6.06, 38.42) * mm, "construction": true});
            skLineSegment(sketch, "E137", {"start": v(-13.4, 42.17) * mm, "end": v(-13.4, 42.82) * mm, "construction": true});
            skLineSegment(sketch, "E138.0.MirrorCS", {"start": v(-20.75, 45.92) * mm, "end": v(-20.75, 38.42) * mm, "construction": true});
            skLineSegment(sketch, "E139", {"start": v(19.72, 10.51) * mm, "end": v(19.72, -4.91) * mm, "construction": true});
            skLineSegment(sketch, "E140", {"start": v(13.22, 10.51) * mm, "end": v(13.22, -4.91) * mm, "construction": true});
            skLineSegment(sketch, "E141", {"start": v(19.72, 2.8) * mm, "end": v(13.22, 2.8) * mm, "construction": true});
            skLineSegment(sketch, "E142", {"start": v(16.47, 2.8) * mm, "end": v(16.47, -8.08) * mm, "construction": true});
            skLineSegment(sketch, "E143", {"start": v(19.72, -4.91) * mm, "end": v(13.22, -4.91) * mm, "construction": true});
            skLineSegment(sketch, "E144", {"start": v(20.22, -4.53) * mm, "end": v(13.22, -4.53) * mm, "construction": true});
            skLineSegment(sketch, "E145", {"start": v(20.22, 10.14) * mm, "end": v(20.22, -4.53) * mm});
            skLineSegment(sketch, "E146", {"start": v(19.77, 10.51) * mm, "end": v(19.72, 10.51) * mm, "construction": true});
            skLineSegment(sketch, "E147", {"start": v(20.22, 10.14) * mm, "end": v(19.73, 10.14) * mm, "construction": true});
            skLineSegment(sketch, "E148.0.MirrorCS", {"start": v(12.72, 10.14) * mm, "end": v(12.72, -4.53) * mm});
            skLineSegment(sketch, "E149.rect.bottom", {"start": v(24.33, 57.12) * mm, "end": v(9.1, 57.12) * mm, "construction": true});
            skLineSegment(sketch, "E149.rect.top", {"start": v(24.33, 26.72) * mm, "end": v(9.1, 26.72) * mm, "construction": true});
            skLineSegment(sketch, "E149.rect.left", {"start": v(24.33, 57.12) * mm, "end": v(24.33, 26.72) * mm, "construction": true});
            skLineSegment(sketch, "E149.rect.right", {"start": v(9.1, 57.12) * mm, "end": v(9.1, 26.72) * mm, "construction": true});
            skCircle(sketch, "E150", {"center": v(9.1, 26.72) * mm, "radius": 1 * mm});
            skCircle(sketch, "E151", {"center": v(24.33, 26.72) * mm, "radius": 1 * mm});
            skCircle(sketch, "E152", {"center": v(9.1, 57.12) * mm, "radius": 1 * mm});
            skCircle(sketch, "E153", {"center": v(24.33, 57.12) * mm, "radius": 1 * mm});
            skLineSegment(sketch, "E154.rect.bottom", {"start": v(24.72, 29.72) * mm, "end": v(21.89, 29.72) * mm});
            skLineSegment(sketch, "E154.rect.top", {"start": v(24.72, 23.72) * mm, "end": v(8.72, 23.72) * mm});
            skLineSegment(sketch, "E154.rect.left", {"start": v(26.72, 27.72) * mm, "end": v(26.72, 25.72) * mm});
            skLineSegment(sketch, "E154.rect.right", {"start": v(6.72, 27.72) * mm, "end": v(6.72, 25.72) * mm});
            skPoint(sketch, "E154.rect.middle", {"position": v(16.72, 26.72) * mm});
            skPoint(sketch, "E155.visualSharp", {"position": v(6.72, 23.72) * mm});
            skArc(sketch, "E155.filletArc", {"start": v(6.72, 25.72) * mm, "mid": v(7.3, 24.3) * mm, "end": v(8.72, 23.72) * mm});
            skPoint(sketch, "E156.visualSharp", {"position": v(6.72, 29.72) * mm});
            skArc(sketch, "E156.filletArc", {"start": v(8.72, 29.72) * mm, "mid": v(7.3, 29.13) * mm, "end": v(6.72, 27.72) * mm});
            skPoint(sketch, "E157.visualSharp", {"position": v(26.72, 29.72) * mm});
            skArc(sketch, "E157.filletArc", {"start": v(26.72, 27.72) * mm, "mid": v(26.13, 29.13) * mm, "end": v(24.72, 29.72) * mm});
            skPoint(sketch, "E158.visualSharp", {"position": v(26.72, 23.72) * mm});
            skArc(sketch, "E158.filletArc", {"start": v(24.72, 23.72) * mm, "mid": v(26.13, 24.3) * mm, "end": v(26.72, 25.72) * mm});
            skLineSegment(sketch, "E159.rect.bottom", {"start": v(24.72, 60.12) * mm, "end": v(8.72, 60.12) * mm});
            skLineSegment(sketch, "E159.rect.top", {"start": v(24.72, 54.12) * mm, "end": v(21.89, 54.12) * mm});
            skLineSegment(sketch, "E159.rect.left", {"start": v(26.72, 58.12) * mm, "end": v(26.72, 56.12) * mm});
            skLineSegment(sketch, "E159.rect.right", {"start": v(6.72, 58.12) * mm, "end": v(6.72, 56.12) * mm});
            skPoint(sketch, "E159.rect.middle", {"position": v(16.72, 57.12) * mm});
            skPoint(sketch, "E160.visualSharp", {"position": v(6.72, 54.12) * mm});
            skArc(sketch, "E160.filletArc", {"start": v(6.72, 56.12) * mm, "mid": v(7.3, 54.7) * mm, "end": v(8.72, 54.12) * mm});
            skPoint(sketch, "E161.visualSharp", {"position": v(6.72, 60.12) * mm});
            skArc(sketch, "E161.filletArc", {"start": v(8.72, 60.12) * mm, "mid": v(7.3, 59.53) * mm, "end": v(6.72, 58.12) * mm});
            skPoint(sketch, "E162.visualSharp", {"position": v(26.72, 60.12) * mm});
            skArc(sketch, "E162.filletArc", {"start": v(26.72, 58.12) * mm, "mid": v(26.13, 59.53) * mm, "end": v(24.72, 60.12) * mm});
            skPoint(sketch, "E163.visualSharp", {"position": v(26.72, 54.12) * mm});
            skArc(sketch, "E163.filletArc", {"start": v(24.72, 54.12) * mm, "mid": v(26.13, 54.7) * mm, "end": v(26.72, 56.12) * mm});
            skArc(sketch, "E164", {"start": v(12.72, -4.53) * mm, "mid": v(16.47, -7.04) * mm, "end": v(20.22, -4.53) * mm});
            skArc(sketch, "E165", {"start": v(20.22, 10.14) * mm, "mid": v(16.47, 12.65) * mm, "end": v(12.72, 10.14) * mm});
            skCircle(sketch, "E166", {"center": v(16.72, 41.92) * mm, "radius": 10 * mm});
            skArc(sketch, "E167", {"start": v(-6.06, 38.42) * mm, "mid": v(-3.02, 42.17) * mm, "end": v(-6.06, 45.92) * mm});
            skArc(sketch, "E168", {"start": v(-20.75, 45.92) * mm, "mid": v(-23.8, 42.17) * mm, "end": v(-20.75, 38.42) * mm});
            skArc(sketch, "E169", {"start": v(11.55, 29.72) * mm, "mid": v(16.72, 28.67) * mm, "end": v(21.89, 29.72) * mm});
            skLineSegment(sketch, "E170.trimOffspring", {"start": v(11.55, 54.12) * mm, "end": v(8.72, 54.12) * mm});
            skLineSegment(sketch, "E171.trimOffspring", {"start": v(11.55, 29.72) * mm, "end": v(8.72, 29.72) * mm});
            skArc(sketch, "E172.trimOffspring", {"start": v(21.89, 54.12) * mm, "mid": v(16.72, 55.17) * mm, "end": v(11.55, 54.12) * mm});
            skSolve(sketch);
        }
        {
            var Q0;
            {var subQ3=sQuery(id+"F6.wireOp",EDGE,"E73.bottom");Q0=makeQuery(id+"F6.imprint","IMPRINT",FACE,{"disambiguationData":[TD([[makeQuery(id+"F6.imprint","IMPRINT",EDGE,{"derivedFrom":subQ3}),1.0]])]});}
            var Q1;
            Q1=makeQuery(id+"F6.imprint","IMPRINT",FACE,{"disambiguationData":[TD([[makeQuery(id+"F6.imprint","IMPRINT",EDGE,{"derivedFrom":sQuery(id+"F6.wireOp",EDGE,"E87.right")}),1.0]])]});
            var Q2;
            Q2=makeQuery(id+"F6.imprint","IMPRINT",FACE,{"disambiguationData":[TD([[makeQuery(id+"F6.imprint","IMPRINT",EDGE,{"derivedFrom":sQuery(id+"F6.wireOp",EDGE,"E77.bottom")}),-1.0]])]});
            var Q3;
            Q3=makeQuery(id+"F6.imprint","IMPRINT",FACE,{"disambiguationData":[TD([[makeQuery(id+"F6.imprint","IMPRINT",EDGE,{"derivedFrom":sQuery(id+"F6.wireOp",EDGE,"E85.trimOffspring")}),1.0]])]});
            var Q4;
            Q4=qCreatedBy(makeId("Top.planeOp"),FACE);
            extrude(context, id + "F12", {"entities" : qUnion([Q0, Q1, Q2, Q3]), "oppositeDirection" : true, "endBoundEntity" : qUnion([Q4]), "depth" : 20 * mm});
        }
        {
            var Q0;
            Q0=makeQuery(id+"F11.imprint","IMPRINT",FACE,{"disambiguationData":[TD([[makeQuery(id+"F11.imprint","IMPRINT",EDGE,{"derivedFrom":sQuery(id+"F11.wireOp",EDGE,"E131.4")}),-1.0]])]});
            var Q1;
            {var subQ3=sQuery(id+"F6.wireOp",EDGE,"E66.5");var subQ5=sQuery(id+"F6.wireOp",EDGE,"E69.0");var subQ8=makeQuery(id+"F6.imprint","INTERSECT",VERTEX,{"derivedFrom":[subQ3,subQ5]});Q1=makeQuery(id+"F6.imprint","IMPRINT",FACE,{"disambiguationData":[TD([[makeQuery(id+"F6.imprint","IMPRINT",EDGE,{"disambiguationData":[TD([[subQ8,-1.0]])],"derivedFrom":subQ3}),1.0]])]});}
            var Q2;
            {var subQ1=sQuery(id+"F6.wireOp",EDGE,"E66.5");var subQ5=sQuery(id+"F6.wireOp",EDGE,"E69.0");var subQ6=makeQuery(id+"F6.imprint","INTERSECT",VERTEX,{"derivedFrom":[subQ1,subQ5]});Q2=makeQuery(id+"F6.imprint","IMPRINT",FACE,{"disambiguationData":[TD([[makeQuery(id+"F6.imprint","IMPRINT",EDGE,{"disambiguationData":[TD([[subQ6,-1.0]])],"derivedFrom":subQ1}),-1.0]])]});}
            var Q3;
            {var subQ0=sQuery(id+"F6.wireOp",EDGE,"E117.trimOffspring");var subQ1=sQuery(id+"F6.wireOp",EDGE,"E66.6");var subQ2=makeQuery(id+"F6.imprint","INTERSECT",VERTEX,{"derivedFrom":[subQ1,subQ0]});Q3=makeQuery(id+"F6.imprint","IMPRINT",FACE,{"disambiguationData":[TD([[makeQuery(id+"F6.imprint","IMPRINT",EDGE,{"disambiguationData":[TD([[subQ2,-1.0]])],"derivedFrom":subQ1}),-1.0]])]});}
            var Q4;
            {var subQ0=sQuery(id+"F6.wireOp",EDGE,"E117.trimOffspring");var subQ1=sQuery(id+"F6.wireOp",EDGE,"E66.6");var subQ2=makeQuery(id+"F6.imprint","INTERSECT",VERTEX,{"derivedFrom":[subQ1,subQ0]});Q4=makeQuery(id+"F6.imprint","IMPRINT",FACE,{"disambiguationData":[TD([[makeQuery(id+"F6.imprint","IMPRINT",EDGE,{"disambiguationData":[TD([[subQ2,-1.0]])],"derivedFrom":subQ1}),1.0]])]});}
            var Q5;
            {var subQ0=sQuery(id+"F6.wireOp",EDGE,"E70.0");var subQ1=sQuery(id+"F6.wireOp",EDGE,"E66.4");var subQ2=makeQuery(id+"F6.imprint","INTERSECT",VERTEX,{"derivedFrom":[subQ1,subQ0]});Q5=makeQuery(id+"F6.imprint","IMPRINT",FACE,{"disambiguationData":[TD([[makeQuery(id+"F6.imprint","IMPRINT",EDGE,{"disambiguationData":[TD([[subQ2,-1.0]])],"derivedFrom":subQ1}),-1.0]])]});}
            var Q6;
            {var subQ1=sQuery(id+"F6.wireOp",EDGE,"E66.7");var subQ5=sQuery(id+"F6.wireOp",EDGE,"E70.0");var subQ6=makeQuery(id+"F6.imprint","INTERSECT",VERTEX,{"derivedFrom":[subQ1,subQ5]});Q6=makeQuery(id+"F6.imprint","IMPRINT",FACE,{"disambiguationData":[TD([[makeQuery(id+"F6.imprint","IMPRINT",EDGE,{"disambiguationData":[TD([[subQ6,-1.0]])],"derivedFrom":subQ1}),1.0]])]});}
            var Q7;
            Q7=makeQuery(id+"F11.imprint","IMPRINT",FACE,{"disambiguationData":[TD([[makeQuery(id+"F11.imprint","IMPRINT",EDGE,{"derivedFrom":sQuery(id+"F11.wireOp",EDGE,"E150")}),-1.0]])]});
            var Q8;
            Q8=makeQuery(id+"F11.imprint","IMPRINT",FACE,{"disambiguationData":[TD([[makeQuery(id+"F11.imprint","IMPRINT",EDGE,{"derivedFrom":sQuery(id+"F11.wireOp",EDGE,"E152")}),-1.0]])]});
            var Q9;
            Q9=makeQuery(id+"F11.imprint","IMPRINT",FACE,{"disambiguationData":[TD([[makeQuery(id+"F11.imprint","IMPRINT",EDGE,{"derivedFrom":makeQuery(id+"F6.imprint","IMPRINT",EDGE,{"derivedFrom":sQuery(id+"F6.wireOp",EDGE,"E85.trimOffspring")})}),1.0]])]});
            var Q10;
            Q10=makeQuery(id+"F11.imprint","IMPRINT",FACE,{"disambiguationData":[TD([[makeQuery(id+"F11.imprint","IMPRINT",EDGE,{"derivedFrom":makeQuery(id+"F6.imprint","IMPRINT",EDGE,{"derivedFrom":sQuery(id+"F6.wireOp",EDGE,"E87.right")})}),1.0]])]});
            var Q11;
            {var subQ3=sQuery(id+"F6.wireOp",EDGE,"E73.bottom");Q11=makeQuery(id+"F11.imprint","IMPRINT",FACE,{"disambiguationData":[TD([[makeQuery(id+"F11.imprint","IMPRINT",EDGE,{"derivedFrom":makeQuery(id+"F6.imprint","IMPRINT",EDGE,{"derivedFrom":subQ3})}),1.0]])]});}
            var Q12;
            Q12=makeQuery(id+"F11.imprint","IMPRINT",FACE,{"disambiguationData":[TD([[makeQuery(id+"F11.imprint","IMPRINT",EDGE,{"derivedFrom":sQuery(id+"F11.wireOp",EDGE,"E150")}),1.0]])]});
            var Q13;
            Q13=makeQuery(id+"F11.imprint","IMPRINT",FACE,{"disambiguationData":[TD([[makeQuery(id+"F11.imprint","IMPRINT",EDGE,{"derivedFrom":sQuery(id+"F11.wireOp",EDGE,"E151")}),1.0]])]});
            var Q14;
            Q14=makeQuery(id+"F11.imprint","IMPRINT",FACE,{"disambiguationData":[TD([[makeQuery(id+"F11.imprint","IMPRINT",EDGE,{"derivedFrom":sQuery(id+"F11.wireOp",EDGE,"E152")}),1.0]])]});
            var Q15;
            Q15=makeQuery(id+"F11.imprint","IMPRINT",FACE,{"disambiguationData":[TD([[makeQuery(id+"F11.imprint","IMPRINT",EDGE,{"derivedFrom":sQuery(id+"F11.wireOp",EDGE,"E153")}),1.0]])]});
            var Q16;
            Q16=qCreatedBy(id+"F2.planeOp",FACE);
            extrude(context, id + "F13", {"entities" : qUnion([Q0, Q1, Q2, Q3, Q4, Q5, Q6, Q7, Q8, Q9, Q10, Q11, Q12, Q13, Q14, Q15]), "oppositeDirection" : true, "endBoundEntity" : qUnion([Q16]), "depth" : 2 * mm});
        }
        {
            var Q0;
            Q0=makeQuery(id+"F11.imprint","IMPRINT",FACE,{"disambiguationData":[TD([[makeQuery(id+"F11.imprint","IMPRINT",EDGE,{"derivedFrom":sQuery(id+"F11.wireOp",EDGE,"E150")}),-1.0]])]});
            var Q1;
            Q1=makeQuery(id+"F11.imprint","IMPRINT",FACE,{"disambiguationData":[TD([[makeQuery(id+"F11.imprint","IMPRINT",EDGE,{"derivedFrom":sQuery(id+"F11.wireOp",EDGE,"E152")}),-1.0]])]});
            extrude(context, id + "F14", {"entities" : qUnion([Q0, Q1]), "operationType" : NewBodyOperationType.ADD, "oppositeDirection" : true, "depth" : 17 * mm});
        }
        {
            var Q0;
            Q0=makeQuery(id+"F7.opExtrude","CAP_EDGE",EDGE,{"disambiguationData":[OSD([sQuery(id+"F6.wireOp",EDGE,"E66.1")])],"isStart":true});
            var Q1;
            Q1=makeQuery(id+"F7.opExtrude","CAP_EDGE",EDGE,{"disambiguationData":[OSD([sQuery(id+"F6.wireOp",EDGE,"E66.26")])],"isStart":true});
            var Q2;
            Q2=makeQuery(id+"F7.opExtrude","CAP_EDGE",EDGE,{"disambiguationData":[OSD([sQuery(id+"F6.wireOp",EDGE,"E66.19")])],"isStart":true});
            var Q3;
            Q3=makeQuery(id+"F7.opExtrude","CAP_EDGE",EDGE,{"disambiguationData":[OSD([sQuery(id+"F6.wireOp",EDGE,"E66.2")])],"isStart":true});
            var Q4;
            Q4=makeQuery(id+"F7.opExtrude","CAP_EDGE",EDGE,{"disambiguationData":[OSD([sQuery(id+"F6.wireOp",EDGE,"E66.28")])],"isStart":true});
            var Q5;
            Q5=makeQuery(id+"F7.opExtrude","CAP_EDGE",EDGE,{"disambiguationData":[OSD([sQuery(id+"F6.wireOp",EDGE,"E66.18")])],"isStart":true});
            var Q6;
            Q6=makeQuery(id+"F7.opExtrude","CAP_EDGE",EDGE,{"disambiguationData":[OSD([sQuery(id+"F6.wireOp",EDGE,"E66.3")])],"isStart":true});
            var Q7;
            Q7=makeQuery(id+"F7.opExtrude","CAP_EDGE",EDGE,{"disambiguationData":[OSD([sQuery(id+"F6.wireOp",EDGE,"E66.16")])],"isStart":true});
            var Q8;
            Q8=makeQuery(id+"F7.opExtrude","CAP_EDGE",EDGE,{"disambiguationData":[OSD([sQuery(id+"F6.wireOp",EDGE,"E66.0")])],"isStart":true});
            var Q9;
            Q9=makeQuery(id+"F7.opExtrude","CAP_EDGE",EDGE,{"disambiguationData":[OSD([sQuery(id+"F6.wireOp",EDGE,"E66.17")])],"isStart":true});
            fillet(context, id + "F15", {"entities" : qUnion([Q0, Q1, Q2, Q3, Q4, Q5, Q6, Q7, Q8, Q9]), "radius" : 1 * mm, "tangentPropagation" : true, "allowEdgeOverflow" : false});
        }
        {
            var Q0;
            Q0=makeQuery(id+"F13.opExtrude","CAP_EDGE",EDGE,{"disambiguationData":[OSD([sQuery(id+"F11.wireOp",EDGE,"E168")])],"isStart":false});
            var Q1;
            Q1=makeQuery(id+"F13.opExtrude","CAP_EDGE",EDGE,{"disambiguationData":[OSD([sQuery(id+"F11.wireOp",EDGE,"E167")])],"isStart":false});
            var Q2;
            Q2=makeQuery(id+"F13.opExtrude","CAP_EDGE",EDGE,{"disambiguationData":[OSD([sQuery(id+"F11.wireOp",EDGE,"E165")])],"isStart":false});
            var Q3;
            Q3=makeQuery(id+"F13.opExtrude","CAP_EDGE",EDGE,{"disambiguationData":[OSD([sQuery(id+"F11.wireOp",EDGE,"E131.4")])],"isStart":false});
            var Q4;
            Q4=makeQuery(id+"F13.opExtrude","CAP_EDGE",EDGE,{"disambiguationData":[OSD([sQuery(id+"F11.wireOp",EDGE,"E164")])],"isStart":false});
            chamfer(context, id + "F16", {"entities" : qUnion([Q0, Q1, Q2, Q3, Q4]), "chamferType" : ChamferType.OFFSET_ANGLE, "width" : 1 * mm, "oppositeDirection" : false, "angle" : 45 * degree, "tangentPropagation" : true});
        }
    });
